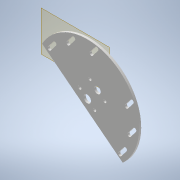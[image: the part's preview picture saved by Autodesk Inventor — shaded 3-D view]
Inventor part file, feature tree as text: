
AUTODESK INVENTOR PART (.ipt)
format: ipt  version: 2022 (Build 260153000, 153)  size: 198,656 bytes
history: native  units: mm
features: reference x10, other x5, extrude x2, sketch x2, plane x1, fillet x1, projected_geometry x1
ambient origin geometry x8: Origin, YZ Plane, XZ Plane, XY Plane, X Axis, Y Axis, Z Axis, Center Point
bodies: Volumenkörper1 (feature_tree)
feature tree (22):
  plane  "Arbeitsebene1"
  extrude  "Extrusion1"  Depth=2.0mm
  extrude  "Extrusion2"  Depth=5.0mm
  fillet  "Rundung1"  Radius=2.8mm
  sketch  "Skizze1"  dims[d0=2.0mm d1=0.0mm d2=2.8mm]
  reference  "Referenz1"
  reference  "Referenz2"
  reference  "Referenz3"
  reference  "Referenz4"
  reference  "Referenz5"
  reference  "Referenz6"
  reference  "Referenz7"
  reference  "Referenz8"
  reference  "Referenz9"
  reference  "Referenz10"
  sketch  "Skizze2"  dims[d3=2.8mm d4=2.8mm d5=2.8mm d6=4.0mm d7=3.1mm d8=3.1mm d9=3.1mm d10=3.1mm d11=3.1mm d12=3.1mm d13=3.1mm d14=2.0mm d15=0.0mm d16=5.0mm]
  projected_geometry  "Projizierte Kontur1"
  other  "Anglerfish_bonne_mamman_m12large_flipped_v0.iam"
  other  "Anglerfish_Lightplate_Tosslink_flipped:1"
  other  "Matchboxscope_M12_Lensadapter_v0:1"
  other  "00_toslink_launcher_v3:2"
  other  "00_toslink_launcher_v3:1"
